# Revit family: LTD-140
name_source: partatom
category: Осветительные приборы
revit_build: Autodesk Revit 2017 (Build: 20160225_1515(x64)
units: mm (PartAtom-declared; Revit-internal decimal feet)

## family parameters
Источник света = Да
Общий = Нет
Основа = Грань
При загрузке вырезать с полостями = Нет
Размер круглого соединителя = Использовать диаметр
Тип детали = Нормальный
Точка расчета площади = Нет

## types (3) — shared parameters
ADSK_Единица измерения = шт.
ADSK_Завод-изготовитель = ARLIGHT
ADSK_Классификация нагрузок = Освещение
ADSK_Количество фаз = 1
ADSK_Количество фаз числовое = 1
ADSK_Коэффициент мощности = 0.98
ADSK_Масса_Текст = 0.95
ADSK_Наименование = Светодиодный светильник
ADSK_Напряжение = 230 В
ADSK_Номинальная мощность = 25 Вт
ADSK_Полная мощность = 26 В·А
ADSK_Размер_Высота = 115 мм
ADSK_Размер_Диаметр = 150 мм
ADSK_Ток = 0 А
ARL_Драйвер = Встроенный (21-35V, 350mA)
ARL_Индекс цветопередачи = >80
ARL_Класс защиты от поражения электрическим током = II
ARL_Класс пылевлагозащиты = IP20
ARL_Материал корпуса = Металл, белый
ARL_Область использования = Для освещения жилых, офисных, торговых и других помещений
ARL_Обозначение корпуса = Корпус круглый, металл, цвет белый
ARL_Рабочая температура окружающей среды = -10...+40 °C
ARL_Серия = LTD NARROW
ARL_Способ монтажа = Встраиваемый
ARL_Тип товара = Светильник
ARL_Угол обзора = 30°
ARL_Цвет покрытия = Белый
URL = https://arlight.ru
Видимая форма излучения при визуализации = Нет
Группа модели = Светильники
Изготовитель = ARLIGHT
Изготовитель (сайт) = www.arlight.ru
Изготовитель (телефон) = 8 800 505 26 29
Излучение по диаметру окружности = 82 мм
Отметка по умолчанию = 1219 мм
Полная установленная мощность = 26 В·А
Разработчик = НТЦ Конструктор
Разработчик (URL) = https://constructor.ru
Разработчик (телефон) = +7 (495) 781-05-35
Светофильтр = 16777215
Смещение цветовой температуры при затухании лампы = <Нет>
Угол наклона = 90.00°

## per-type parameters (varying)
| type | ADSK_Код изделия | ADSK_Марка | ARL_Цвет свечения | Комментарии к типоразмеру | Описание | Файл фотометрической сетки |
| 032618 Светодиодный светильник LTD-140WH 25W Warm White 30deg | Арт. 032618 | LTD-140WH 25W Warm White 30deg | Теплый 3000K | Арт. 032618 | Встраиваемый круглый светильник с наклоняемой осью, угол 30° / 25 Вт / ТЕПЛЫЙ БЕЛЫЙ 3000K / светодиод 1x25W CREE / 1950 лм. Белая лицевая панель. Питание AC110-240V, драйвер в комплекте 600mA 34-50V). Размеры DxH: 150х115 мм, отверстие для установки 128 мм | 032618_LTD-140WH 25W Warm White 30deg.ies |
| 032619 Светодиодный светильник LTD-140WH 25W Day White 30deg | Арт. 032619 | LTD-140WH 25W Day White 30deg | Дневной 4500K | Арт. 032619 | Встраиваемый круглый светильник с наклоняемой осью, угол 30° / 25 Вт / ДНЕВНОЙ БЕЛЫЙ 4000-4500K / светодиод 1x25W CREE / 1950 лм. Белая лицевая панель. Питание AC110-240V, драйвер в комплекте 600mA 34-50V). Размеры DxH: 150х115 мм, отверстие для установки 128 мм | 032619_LTD-140WH 25W Day White 30deg.ies |
| 032620 Светодиодный светильник LTD-140WH 25W White 30deg | Арт. 032620 | LTD-140WH 25W White 30deg | Дневной 5000K | Арт. 032620 | Встраиваемый круглый светильник с наклоняемой осью, угол 30° / 25 Вт / БЕЛЫЙ 5000K / светодиод 1x25W CREE / 1950 лм. Белая лицевая панель. Питание AC110-240V, драйвер в комплекте 600mA 34-50V). Размеры DxH: 150х115 мм, отверстие для установки 128 мм | 032620_LTD-140WH 25W White 30deg.ies |
